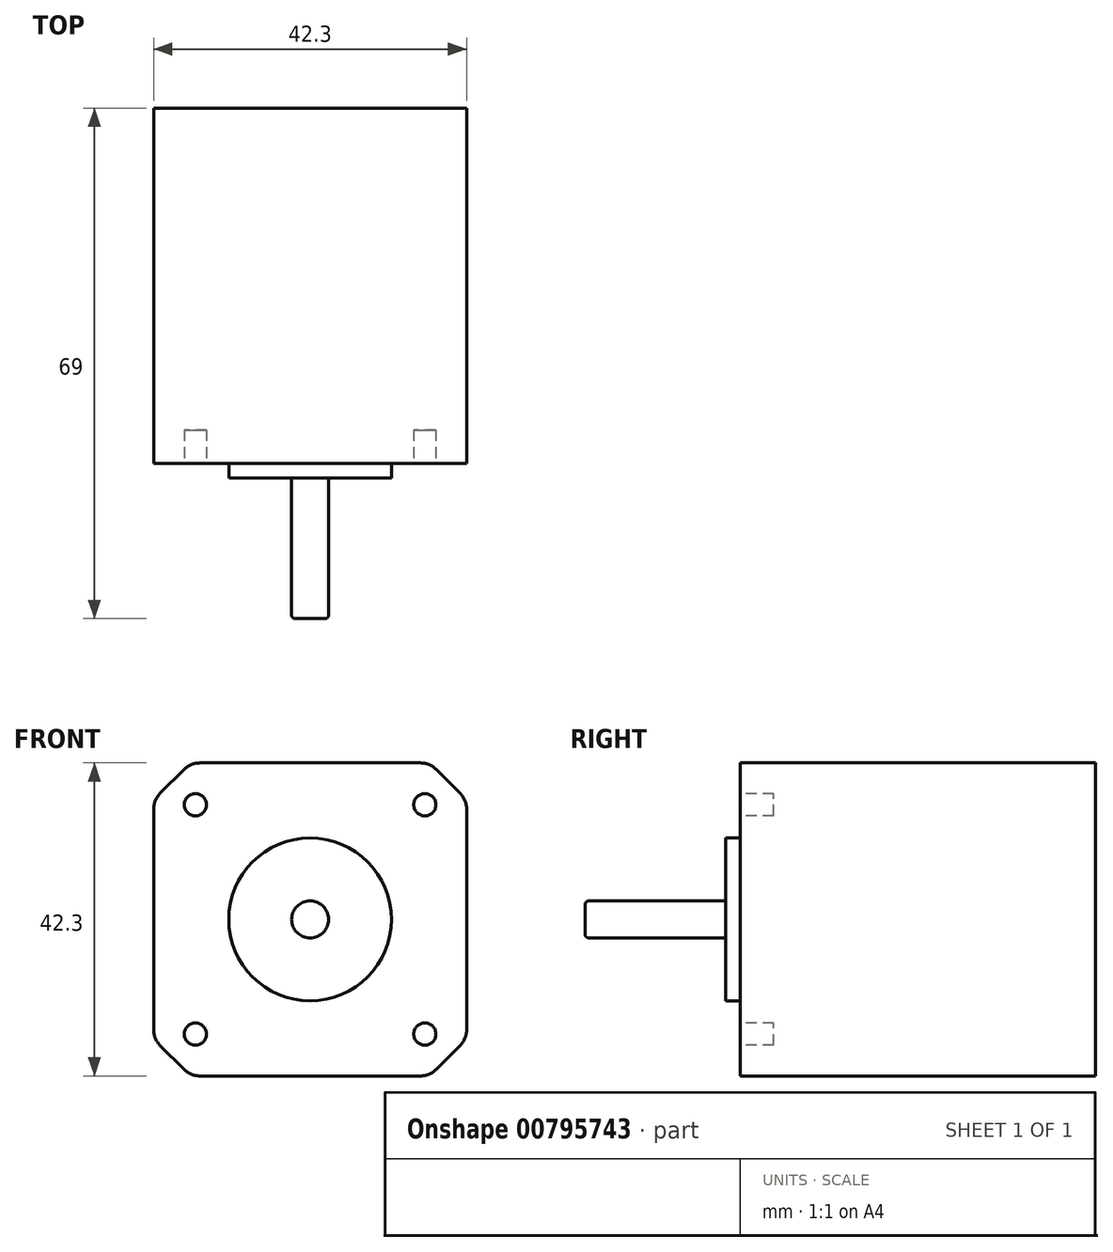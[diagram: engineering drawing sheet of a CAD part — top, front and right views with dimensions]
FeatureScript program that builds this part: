
annotation { "Feature Type Name" : "Feature", "Feature Type Description" : "" }
export const myFeature = defineFeature(function(context is Context, id is Id, definition is map)
    precondition{}
    {
        {
            var Q0;
            Q0=qCreatedBy(makeId("Front.planeOp"),FACE);
            var sketch = newSketch(context, id + "F0", { "sketchPlane" : qUnion([Q0])});
            skLineSegment(sketch, "E0.bottom", {"start": v(21.15, -21.15) * mm, "end": v(-21.15, -21.15) * mm});
            skLineSegment(sketch, "E0.top", {"start": v(21.15, 21.15) * mm, "end": v(-21.15, 21.15) * mm});
            skLineSegment(sketch, "E0.left", {"start": v(21.15, -21.15) * mm, "end": v(21.15, 21.15) * mm});
            skLineSegment(sketch, "E0.right", {"start": v(-21.15, -21.15) * mm, "end": v(-21.15, 21.15) * mm});
            skPoint(sketch, "E0.middle", {"position": v(0, 0) * mm});
            skSolve(sketch);
        }
        {
            var Q0;
            Q0 = qSketchRegion(id + "F0", true);
            extrude(context, id + "F1", {"entities" : qUnion([Q0]), "depth" : 48 * mm, "offsetDistance" : 25 * mm});
        }
        {
            var Q0;
            Q0=makeQuery(id+"F1.opExtrude","CAP_FACE",FACE,{"disambiguationData":[OSD([sQuery(id+"F0.wireOp",EDGE,"E0.bottom"),sQuery(id+"F0.wireOp",EDGE,"E0.top"),sQuery(id+"F0.wireOp",EDGE,"E0.left"),sQuery(id+"F0.wireOp",EDGE,"E0.right")])],"isStart":false});
            var sketch = newSketch(context, id + "F2", { "sketchPlane" : qUnion([Q0])});
            skLineSegment(sketch, "E1", {"start": v(0, 0) * mm, "end": v(0, 15.5) * mm, "construction": true});
            skLineSegment(sketch, "E2", {"start": v(0, 15.5) * mm, "end": v(-15.5, 15.5) * mm, "construction": true});
            skLineSegment(sketch, "E3", {"start": v(-15.5, 15.5) * mm, "end": v(-15.5, -15.5) * mm, "construction": true});
            skLineSegment(sketch, "E4", {"start": v(-15.5, -15.5) * mm, "end": v(15.5, -15.5) * mm, "construction": true});
            skLineSegment(sketch, "E5", {"start": v(15.5, -15.5) * mm, "end": v(15.5, 15.5) * mm, "construction": true});
            skCircle(sketch, "E6", {"center": v(-15.5, 15.5) * mm, "radius": 1.5 * mm});
            skCircle(sketch, "E7", {"center": v(-15.5, -15.5) * mm, "radius": 1.5 * mm});
            skCircle(sketch, "E8", {"center": v(15.5, -15.5) * mm, "radius": 1.5 * mm});
            skCircle(sketch, "E9", {"center": v(15.5, 15.5) * mm, "radius": 1.5 * mm});
            skSolve(sketch);
        }
        {
            var Q0;
            Q0=makeQuery(id+"F2.imprint","IMPRINT",FACE,{"disambiguationData":[TD([[makeQuery(id+"F2.imprint","IMPRINT",EDGE,{"derivedFrom":sQuery(id+"F2.wireOp",EDGE,"E6")}),1.0]])]});
            var Q1;
            Q1=makeQuery(id+"F2.imprint","IMPRINT",FACE,{"disambiguationData":[TD([[makeQuery(id+"F2.imprint","IMPRINT",EDGE,{"derivedFrom":sQuery(id+"F2.wireOp",EDGE,"E7")}),1.0]])]});
            var Q2;
            Q2=makeQuery(id+"F2.imprint","IMPRINT",FACE,{"disambiguationData":[TD([[makeQuery(id+"F2.imprint","IMPRINT",EDGE,{"derivedFrom":sQuery(id+"F2.wireOp",EDGE,"E8")}),1.0]])]});
            var Q3;
            Q3=makeQuery(id+"F2.imprint","IMPRINT",FACE,{"disambiguationData":[TD([[makeQuery(id+"F2.imprint","IMPRINT",EDGE,{"derivedFrom":sQuery(id+"F2.wireOp",EDGE,"E9")}),1.0]])]});
            extrude(context, id + "F3", {"entities" : qUnion([Q0, Q1, Q2, Q3]), "operationType" : NewBodyOperationType.REMOVE, "oppositeDirection" : true, "depth" : 4.5 * mm, "offsetDistance" : 25 * mm});
        }
        {
            var Q0;
            Q0=makeQuery(id+"F1.opExtrude","CAP_FACE",FACE,{"disambiguationData":[OSD([sQuery(id+"F0.wireOp",EDGE,"E0.bottom"),sQuery(id+"F0.wireOp",EDGE,"E0.top"),sQuery(id+"F0.wireOp",EDGE,"E0.left"),sQuery(id+"F0.wireOp",EDGE,"E0.right")])],"isStart":false});
            var sketch = newSketch(context, id + "F4", { "sketchPlane" : qUnion([Q0])});
            skCircle(sketch, "E10", {"center": v(0, 0) * mm, "radius": 11 * mm});
            skSolve(sketch);
        }
        {
            var Q0;
            Q0 = qSketchRegion(id + "F4", true);
            extrude(context, id + "F5", {"entities" : qUnion([Q0]), "operationType" : NewBodyOperationType.ADD, "depth" : 2 * mm, "offsetDistance" : 25 * mm});
        }
        {
            var Q0;
            Q0=makeQuery(id+"F1.opExtrude","SWEPT_EDGE",EDGE,{"disambiguationData":[OSD([sQuery(id+"F0.wireOp",EDGE,"E0.top"),sQuery(id+"F0.wireOp",EDGE,"E0.left")])]});
            var Q1;
            Q1=makeQuery(id+"F1.opExtrude","SWEPT_EDGE",EDGE,{"disambiguationData":[OSD([sQuery(id+"F0.wireOp",EDGE,"E0.top"),sQuery(id+"F0.wireOp",EDGE,"E0.right")])]});
            var Q2;
            Q2=makeQuery(id+"F1.opExtrude","SWEPT_EDGE",EDGE,{"disambiguationData":[OSD([sQuery(id+"F0.wireOp",EDGE,"E0.bottom"),sQuery(id+"F0.wireOp",EDGE,"E0.right")])]});
            var Q3;
            Q3=makeQuery(id+"F1.opExtrude","SWEPT_EDGE",EDGE,{"disambiguationData":[OSD([sQuery(id+"F0.wireOp",EDGE,"E0.bottom"),sQuery(id+"F0.wireOp",EDGE,"E0.left")])]});
            chamfer(context, id + "F6", {"entities" : qUnion([Q0, Q1, Q2, Q3]), "width" : 5 * mm, "tangentPropagation" : true});
        }
        {
            var Q0;
            Q0=makeQuery(id+"F5.opExtrude","CAP_FACE",FACE,{"disambiguationData":[OSD([sQuery(id+"F4.wireOp",EDGE,"E10")])],"isStart":false});
            var sketch = newSketch(context, id + "F7", { "sketchPlane" : qUnion([Q0])});
            skCircle(sketch, "E11", {"center": v(0, 0) * mm, "radius": 2.5 * mm});
            skSolve(sketch);
        }
        {
            var Q0;
            Q0 = qSketchRegion(id + "F7", true);
            extrude(context, id + "F8", {"entities" : qUnion([Q0]), "operationType" : NewBodyOperationType.ADD, "depth" : 19 * mm, "offsetDistance" : 25 * mm});
        }
        {
            var Q0;
            Q0=makeQuery(id+"F8.opExtrude","CAP_EDGE",EDGE,{"disambiguationData":[OSD([sQuery(id+"F7.wireOp",EDGE,"E11")])],"isStart":false});
            fillet(context, id + "F9", {"entities" : qUnion([Q0]), "radius" : 0.5 * mm, "tangentPropagation" : true, "allowEdgeOverflow" : false});
        }
        {
            var Q0;
            {var subQ0=sQuery(id+"F0.wireOp",EDGE,"E0.bottom");Q0=makeQuery(id+"F6.opChamfer","BLEND_EDGE",EDGE,{"blendedFrom":[makeQuery(id+"F1.opExtrude","SWEPT_EDGE",EDGE,{"disambiguationData":[OSD([subQ0,sQuery(id+"F0.wireOp",EDGE,"E0.left")])]}),makeQuery(id+"F1.opExtrude","SWEPT_FACE",FACE,{"disambiguationData":[OSD([subQ0])]})],"blendedInto":[makeQuery(id+"F1.opExtrude","SWEPT_FACE",FACE,{"disambiguationData":[OSD([subQ0])]})]});}
            var Q1;
            {var subQ0=sQuery(id+"F0.wireOp",EDGE,"E0.left");Q1=makeQuery(id+"F6.opChamfer","BLEND_EDGE",EDGE,{"blendedFrom":[makeQuery(id+"F1.opExtrude","SWEPT_EDGE",EDGE,{"disambiguationData":[OSD([sQuery(id+"F0.wireOp",EDGE,"E0.bottom"),subQ0])]}),makeQuery(id+"F1.opExtrude","SWEPT_FACE",FACE,{"disambiguationData":[OSD([subQ0])]})],"blendedInto":[makeQuery(id+"F1.opExtrude","SWEPT_FACE",FACE,{"disambiguationData":[OSD([subQ0])]})]});}
            var Q2;
            {var subQ0=sQuery(id+"F0.wireOp",EDGE,"E0.bottom");Q2=makeQuery(id+"F6.opChamfer","BLEND_EDGE",EDGE,{"blendedFrom":[makeQuery(id+"F1.opExtrude","SWEPT_EDGE",EDGE,{"disambiguationData":[OSD([subQ0,sQuery(id+"F0.wireOp",EDGE,"E0.right")])]}),makeQuery(id+"F1.opExtrude","SWEPT_FACE",FACE,{"disambiguationData":[OSD([subQ0])]})],"blendedInto":[makeQuery(id+"F1.opExtrude","SWEPT_FACE",FACE,{"disambiguationData":[OSD([subQ0])]})]});}
            var Q3;
            {var subQ0=sQuery(id+"F0.wireOp",EDGE,"E0.right");Q3=makeQuery(id+"F6.opChamfer","BLEND_EDGE",EDGE,{"blendedFrom":[makeQuery(id+"F1.opExtrude","SWEPT_EDGE",EDGE,{"disambiguationData":[OSD([sQuery(id+"F0.wireOp",EDGE,"E0.bottom"),subQ0])]}),makeQuery(id+"F1.opExtrude","SWEPT_FACE",FACE,{"disambiguationData":[OSD([subQ0])]})],"blendedInto":[makeQuery(id+"F1.opExtrude","SWEPT_FACE",FACE,{"disambiguationData":[OSD([subQ0])]})]});}
            var Q4;
            {var subQ0=sQuery(id+"F0.wireOp",EDGE,"E0.left");Q4=makeQuery(id+"F6.opChamfer","BLEND_EDGE",EDGE,{"blendedFrom":[makeQuery(id+"F1.opExtrude","SWEPT_EDGE",EDGE,{"disambiguationData":[OSD([sQuery(id+"F0.wireOp",EDGE,"E0.top"),subQ0])]}),makeQuery(id+"F1.opExtrude","SWEPT_FACE",FACE,{"disambiguationData":[OSD([subQ0])]})],"blendedInto":[makeQuery(id+"F1.opExtrude","SWEPT_FACE",FACE,{"disambiguationData":[OSD([subQ0])]})]});}
            var Q5;
            {var subQ0=sQuery(id+"F0.wireOp",EDGE,"E0.top");Q5=makeQuery(id+"F6.opChamfer","BLEND_EDGE",EDGE,{"blendedFrom":[makeQuery(id+"F1.opExtrude","SWEPT_EDGE",EDGE,{"disambiguationData":[OSD([subQ0,sQuery(id+"F0.wireOp",EDGE,"E0.left")])]}),makeQuery(id+"F1.opExtrude","SWEPT_FACE",FACE,{"disambiguationData":[OSD([subQ0])]})],"blendedInto":[makeQuery(id+"F1.opExtrude","SWEPT_FACE",FACE,{"disambiguationData":[OSD([subQ0])]})]});}
            var Q6;
            {var subQ0=sQuery(id+"F0.wireOp",EDGE,"E0.top");Q6=makeQuery(id+"F6.opChamfer","BLEND_EDGE",EDGE,{"blendedFrom":[makeQuery(id+"F1.opExtrude","SWEPT_EDGE",EDGE,{"disambiguationData":[OSD([subQ0,sQuery(id+"F0.wireOp",EDGE,"E0.right")])]}),makeQuery(id+"F1.opExtrude","SWEPT_FACE",FACE,{"disambiguationData":[OSD([subQ0])]})],"blendedInto":[makeQuery(id+"F1.opExtrude","SWEPT_FACE",FACE,{"disambiguationData":[OSD([subQ0])]})]});}
            var Q7;
            {var subQ0=sQuery(id+"F0.wireOp",EDGE,"E0.right");Q7=makeQuery(id+"F6.opChamfer","BLEND_EDGE",EDGE,{"blendedFrom":[makeQuery(id+"F1.opExtrude","SWEPT_EDGE",EDGE,{"disambiguationData":[OSD([sQuery(id+"F0.wireOp",EDGE,"E0.top"),subQ0])]}),makeQuery(id+"F1.opExtrude","SWEPT_FACE",FACE,{"disambiguationData":[OSD([subQ0])]})],"blendedInto":[makeQuery(id+"F1.opExtrude","SWEPT_FACE",FACE,{"disambiguationData":[OSD([subQ0])]})]});}
            fillet(context, id + "F10", {"entities" : qUnion([Q0, Q1, Q2, Q3, Q4, Q5, Q6, Q7]), "radius" : 3 * mm, "tangentPropagation" : true, "allowEdgeOverflow" : false});
        }
    });
